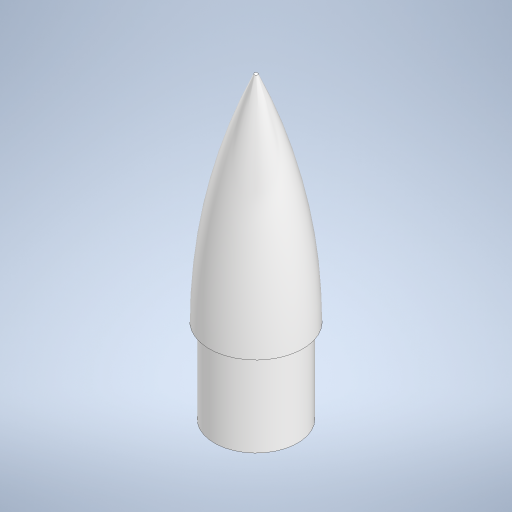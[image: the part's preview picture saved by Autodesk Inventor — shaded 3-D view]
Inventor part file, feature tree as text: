
AUTODESK INVENTOR PART (.ipt)
format: ipt  version: 2024 (Build 280153000, 153)  size: 342,016 bytes
history: native  units: mm
features: sketch x4, other x2, loft x1
ambient origin geometry x8: Origin, YZ Plane, XZ Plane, XY Plane, X Axis, Y Axis, Z Axis, Center Point
bodies: Body1 (feature_tree)
feature tree (7):
  other  "cone_sketch"
  other  "cone_revolve"
  loft  "shock_cord_attachment"
  sketch  "Sketch3"  dims[d1=9.7mm d2=19.6mm]
  sketch  "Sketch4"  dims[d4=1.2mm]
  sketch  "Sketch5"  dims[d6=0.4mm]
  sketch  "Sketch6"  dims[d7=69.6mm d8=19.6mm d9=0.8mm d11=0.8mm d12=0.8mm d13=0.8mm d14=19.6mm d15=1.2mm d16=0.8mm d17=20.4mm d18=0.4mm d19=90.0deg d20=1.2mm d21=3.1mm d22=1.2mm d23=3.1mm d24=3.1mm d25=1.2mm d26=3.1mm d28=0.0mm d29=90.0deg d30=0.0mm d31=90.0deg d32=0.0mm d33=90.0deg d34=0.0mm d35=90.0deg]
